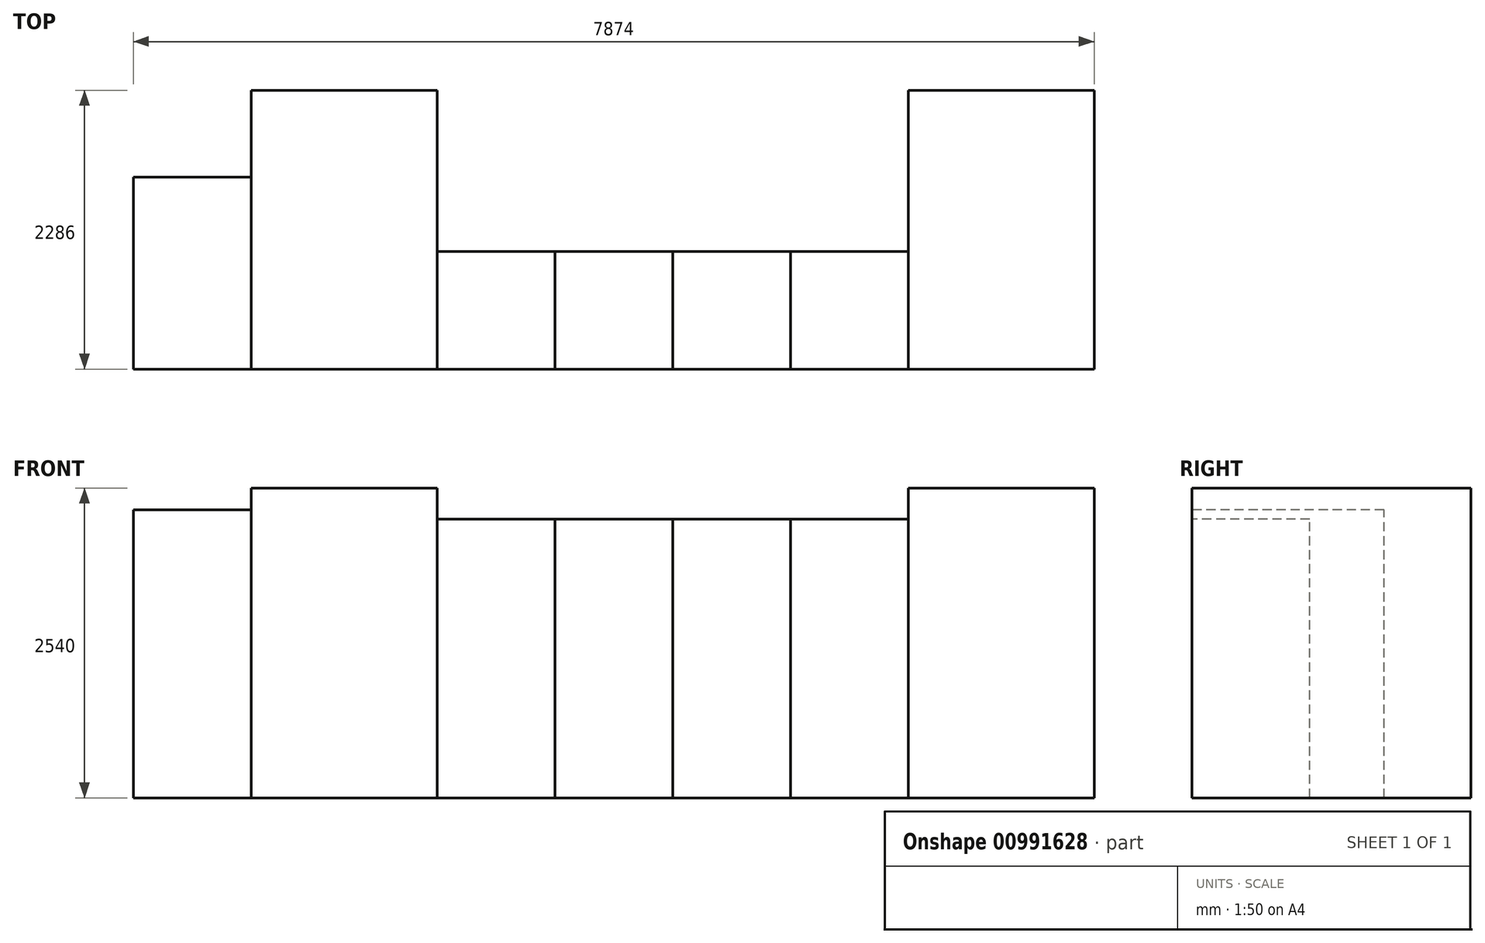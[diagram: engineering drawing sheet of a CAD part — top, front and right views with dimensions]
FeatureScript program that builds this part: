
annotation { "Feature Type Name" : "Feature", "Feature Type Description" : "" }
export const myFeature = defineFeature(function(context is Context, id is Id, definition is map)
    precondition{}
    {
        {
            var Q0;
            Q0=qCreatedBy(makeId("Front.planeOp"),FACE);
            var sketch = newSketch(context, id + "F0", { "sketchPlane" : qUnion([Q0])});
            skLineSegment(sketch, "E0.bottom", {"start": v(0, 0) * mm, "end": v(965.2, 0) * mm});
            skLineSegment(sketch, "E0.top", {"start": v(0, 2362.2) * mm, "end": v(965.2, 2362.2) * mm});
            skLineSegment(sketch, "E0.left", {"start": v(0, 0) * mm, "end": v(0, 2362.2) * mm});
            skLineSegment(sketch, "E0.right", {"start": v(965.2, 0) * mm, "end": v(965.2, 2362.2) * mm});
            skLineSegment(sketch, "E1.bottom", {"start": v(965.2, 0) * mm, "end": v(2489.2, 0) * mm});
            skLineSegment(sketch, "E1.top", {"start": v(965.2, 2540) * mm, "end": v(2489.2, 2540) * mm});
            skLineSegment(sketch, "E1.left", {"start": v(965.2, 0) * mm, "end": v(965.2, 2540) * mm});
            skLineSegment(sketch, "E1.right", {"start": v(2489.2, 0) * mm, "end": v(2489.2, 2540) * mm});
            skLineSegment(sketch, "E2.bottom", {"start": v(2489.2, 0) * mm, "end": v(3454.4, 0) * mm});
            skLineSegment(sketch, "E2.top", {"start": v(2489.2, 2286) * mm, "end": v(3454.4, 2286) * mm});
            skLineSegment(sketch, "E2.left", {"start": v(2489.2, 0) * mm, "end": v(2489.2, 2286) * mm});
            skLineSegment(sketch, "E2.right", {"start": v(3454.4, 0) * mm, "end": v(3454.4, 2286) * mm});
            skLineSegment(sketch, "E3.bottom", {"start": v(3454.4, 2286) * mm, "end": v(4419.6, 2286) * mm});
            skLineSegment(sketch, "E3.top", {"start": v(3454.4, 0) * mm, "end": v(4419.6, 0) * mm});
            skLineSegment(sketch, "E3.left", {"start": v(3454.4, 2286) * mm, "end": v(3454.4, 0) * mm});
            skLineSegment(sketch, "E3.right", {"start": v(4419.6, 2286) * mm, "end": v(4419.6, 0) * mm});
            skLineSegment(sketch, "E4.bottom", {"start": v(4419.6, 0) * mm, "end": v(5384.8, 0) * mm});
            skLineSegment(sketch, "E4.top", {"start": v(4419.6, 2286) * mm, "end": v(5384.8, 2286) * mm});
            skLineSegment(sketch, "E4.left", {"start": v(4419.6, 0) * mm, "end": v(4419.6, 2286) * mm});
            skLineSegment(sketch, "E4.right", {"start": v(5384.8, 0) * mm, "end": v(5384.8, 2286) * mm});
            skLineSegment(sketch, "E5.bottom", {"start": v(5384.8, 2286) * mm, "end": v(6350, 2286) * mm});
            skLineSegment(sketch, "E5.top", {"start": v(5384.8, 0) * mm, "end": v(6350, 0) * mm});
            skLineSegment(sketch, "E5.left", {"start": v(5384.8, 2286) * mm, "end": v(5384.8, 0) * mm});
            skLineSegment(sketch, "E5.right", {"start": v(6350, 2286) * mm, "end": v(6350, 0) * mm});
            skLineSegment(sketch, "E6.bottom", {"start": v(6350, 0) * mm, "end": v(7874, 0) * mm});
            skLineSegment(sketch, "E6.top", {"start": v(6350, 2540) * mm, "end": v(7874, 2540) * mm});
            skLineSegment(sketch, "E6.left", {"start": v(6350, 0) * mm, "end": v(6350, 2540) * mm});
            skLineSegment(sketch, "E6.right", {"start": v(7874, 0) * mm, "end": v(7874, 2540) * mm});
            skSolve(sketch);
        }
        {
            var Q0;
            Q0=makeQuery(id+"F0.imprint","IMPRINT",FACE,{"disambiguationData":[TD([[makeQuery(id+"F0.imprint","IMPRINT",EDGE,{"derivedFrom":sQuery(id+"F0.wireOp",EDGE,"E0.bottom")}),1.0]])]});
            extrude(context, id + "F1", {"entities" : qUnion([Q0]), "oppositeDirection" : true, "depth" : 1574.8 * mm, "offsetDistance" : 25.4 * mm});
        }
        {
            var Q0;
            {var subQ3=sQuery(id+"F0.wireOp",EDGE,"E1.bottom");Q0=makeQuery(id+"F0.imprint","IMPRINT",FACE,{"disambiguationData":[TD([[makeQuery(id+"F0.imprint","IMPRINT",EDGE,{"derivedFrom":subQ3}),1.0]])]});}
            extrude(context, id + "F2", {"entities" : qUnion([Q0]), "oppositeDirection" : true, "depth" : 2286 * mm, "offsetDistance" : 25.4 * mm});
        }
        {
            var Q0;
            Q0=makeQuery(id+"F0.imprint","IMPRINT",FACE,{"disambiguationData":[TD([[makeQuery(id+"F0.imprint","IMPRINT",EDGE,{"derivedFrom":sQuery(id+"F0.wireOp",EDGE,"E2.bottom")}),1.0]])]});
            extrude(context, id + "F3", {"entities" : qUnion([Q0]), "oppositeDirection" : true, "depth" : 965.2 * mm, "offsetDistance" : 25.4 * mm});
        }
        {
            var Q0;
            Q0=makeQuery(id+"F0.imprint","IMPRINT",FACE,{"disambiguationData":[TD([[makeQuery(id+"F0.imprint","IMPRINT",EDGE,{"derivedFrom":sQuery(id+"F0.wireOp",EDGE,"E3.bottom")}),-1.0]])]});
            extrude(context, id + "F4", {"entities" : qUnion([Q0]), "oppositeDirection" : true, "depth" : 965.2 * mm, "offsetDistance" : 25.4 * mm});
        }
        {
            var Q0;
            Q0=makeQuery(id+"F0.imprint","IMPRINT",FACE,{"disambiguationData":[TD([[makeQuery(id+"F0.imprint","IMPRINT",EDGE,{"derivedFrom":sQuery(id+"F0.wireOp",EDGE,"E4.bottom")}),1.0]])]});
            extrude(context, id + "F5", {"entities" : qUnion([Q0]), "oppositeDirection" : true, "depth" : 965.2 * mm, "offsetDistance" : 25.4 * mm});
        }
        {
            var Q0;
            {var subQ0=sQuery(id+"F0.wireOp",EDGE,"E5.bottom");Q0=makeQuery(id+"F0.imprint","IMPRINT",FACE,{"disambiguationData":[TD([[makeQuery(id+"F0.imprint","IMPRINT",EDGE,{"derivedFrom":subQ0}),-1.0]])]});}
            extrude(context, id + "F6", {"entities" : qUnion([Q0]), "oppositeDirection" : true, "depth" : 965.2 * mm, "offsetDistance" : 25.4 * mm});
        }
        {
            var Q0;
            {var subQ3=sQuery(id+"F0.wireOp",EDGE,"E6.bottom");Q0=makeQuery(id+"F0.imprint","IMPRINT",FACE,{"disambiguationData":[TD([[makeQuery(id+"F0.imprint","IMPRINT",EDGE,{"derivedFrom":subQ3}),1.0]])]});}
            extrude(context, id + "F7", {"entities" : qUnion([Q0]), "oppositeDirection" : true, "depth" : 2286 * mm, "offsetDistance" : 25.4 * mm});
        }
    });
